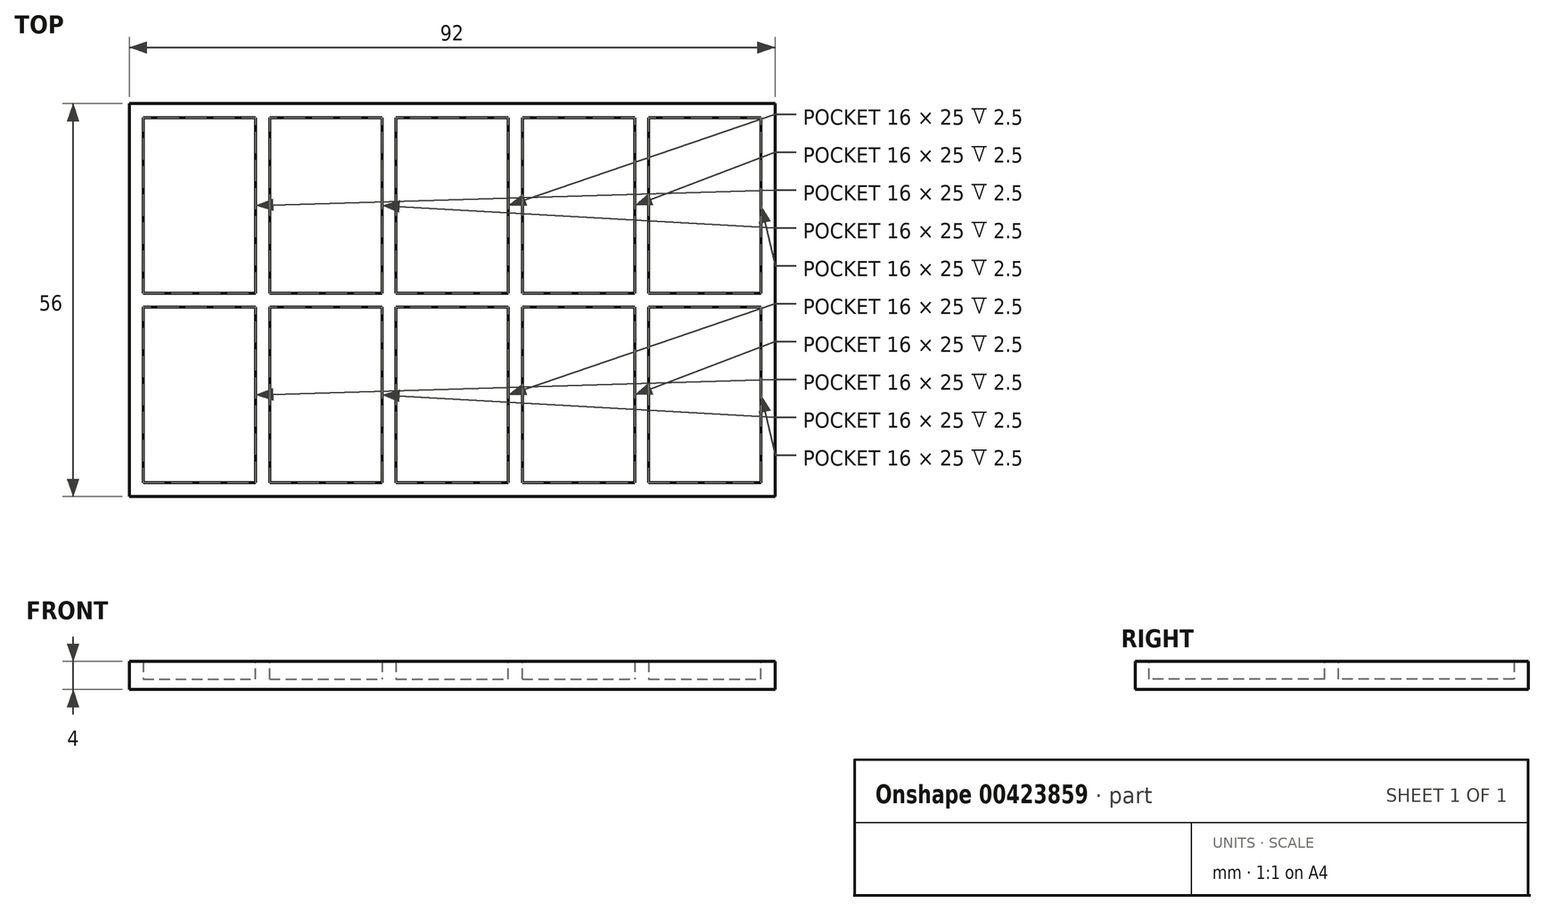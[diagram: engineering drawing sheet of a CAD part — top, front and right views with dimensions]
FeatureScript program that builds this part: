
annotation { "Feature Type Name" : "Feature", "Feature Type Description" : "" }
export const myFeature = defineFeature(function(context is Context, id is Id, definition is map)
    precondition{}
    {
        {
            var Q0;
            Q0=qCreatedBy(makeId("Top.planeOp"),FACE);
            var sketch = newSketch(context, id + "F0", { "sketchPlane" : qUnion([Q0])});
            skLineSegment(sketch, "E0.bottom", {"start": v(46, 28) * mm, "end": v(-46, 28) * mm});
            skLineSegment(sketch, "E0.top", {"start": v(46, -28) * mm, "end": v(-46, -28) * mm});
            skLineSegment(sketch, "E0.left", {"start": v(46, 28) * mm, "end": v(46, -28) * mm});
            skLineSegment(sketch, "E0.right", {"start": v(-46, 28) * mm, "end": v(-46, -28) * mm});
            skPoint(sketch, "E0.middle", {"position": v(0, 0) * mm});
            skSolve(sketch);
        }
        {
            var Q0;
            Q0=makeQuery(id+"F0.imprint","IMPRINT",FACE,{"disambiguationData":[TD([[makeQuery(id+"F0.imprint","IMPRINT",EDGE,{"derivedFrom":sQuery(id+"F0.wireOp",EDGE,"E0.bottom")}),1.0]])]});
            var Q1;
            Q1 = qSketchRegion(id + "F2", true);
            extrude(context, id + "F1", {"entities" : qUnion([Q0, Q1]), "depth" : 1.5 * mm, "offsetDistance" : 25 * mm});
        }
        {
            var Q0;
            Q0=qCreatedBy(makeId("Top.planeOp"),FACE);
            var sketch = newSketch(context, id + "F2", { "sketchPlane" : qUnion([Q0])});
            skLineSegment(sketch, "E1.bottom", {"start": v(46, -28) * mm, "end": v(44, -28) * mm});
            skLineSegment(sketch, "E1.top", {"start": v(46, 28) * mm, "end": v(44, 28) * mm});
            skLineSegment(sketch, "E1.left", {"start": v(46, -28) * mm, "end": v(46, 28) * mm});
            skLineSegment(sketch, "E1.right", {"start": v(44, -28) * mm, "end": v(44, 28) * mm});
            skSolve(sketch);
        }
        {
            var Q0;
            Q0 = qSketchRegion(id + "F2", true);
            extrude(context, id + "F3", {"entities" : qUnion([Q0]), "depth" : 4 * mm, "offsetDistance" : 25 * mm});
        }
        {
            var Q0;
            Q0=makeQuery(id+"F3.opExtrude","SWEPT_BODY",BODY,{"disambiguationData":[OSD([sQuery(id+"F2.wireOp",EDGE,"E1.bottom"),sQuery(id+"F2.wireOp",EDGE,"E1.top"),sQuery(id+"F2.wireOp",EDGE,"E1.left"),sQuery(id+"F2.wireOp",EDGE,"E1.right")])]});
            var Q1;
            Q1=qCreatedBy(makeId("Right.planeOp"),FACE);
            mirror(context, id + "F4", {"operationType" : NewBodyOperationType.ADD, "entities" : qUnion([Q0]), "mirrorPlane" : qUnion([Q1])});
        }
        {
            var Q0;
            Q0=qCreatedBy(makeId("Top.planeOp"),FACE);
            var sketch = newSketch(context, id + "F5", { "sketchPlane" : qUnion([Q0])});
            skLineSegment(sketch, "E2.bottom", {"start": v(-46, -28) * mm, "end": v(46, -28) * mm});
            skLineSegment(sketch, "E2.top", {"start": v(-46, -26) * mm, "end": v(46, -26) * mm});
            skLineSegment(sketch, "E2.left", {"start": v(-46, -28) * mm, "end": v(-46, -26) * mm});
            skLineSegment(sketch, "E2.right", {"start": v(46, -28) * mm, "end": v(46, -26) * mm});
            skSolve(sketch);
        }
        {
            var Q0;
            Q0 = qSketchRegion(id + "F5", true);
            extrude(context, id + "F6", {"entities" : qUnion([Q0]), "operationType" : NewBodyOperationType.ADD, "depth" : 4 * mm, "offsetDistance" : 25 * mm});
        }
        {
            var Q0;
            Q0=makeQuery(id+"F1.opExtrude","SWEPT_BODY",BODY,{"disambiguationData":[OSD([sQuery(id+"F0.wireOp",EDGE,"E0.bottom"),sQuery(id+"F0.wireOp",EDGE,"E0.top"),sQuery(id+"F0.wireOp",EDGE,"E0.left"),sQuery(id+"F0.wireOp",EDGE,"E0.right")])]});
            var Q1;
            Q1=qCreatedBy(makeId("Front.planeOp"),FACE);
            mirror(context, id + "F7", {"operationType" : NewBodyOperationType.ADD, "entities" : qUnion([Q0]), "mirrorPlane" : qUnion([Q1])});
        }
        {
            var Q0;
            Q0=qCreatedBy(makeId("Top.planeOp"),FACE);
            var sketch = newSketch(context, id + "F8", { "sketchPlane" : qUnion([Q0])});
            skLineSegment(sketch, "E3.bottom", {"start": v(26, 28) * mm, "end": v(28, 28) * mm});
            skLineSegment(sketch, "E3.top", {"start": v(26, -28) * mm, "end": v(28, -28) * mm});
            skLineSegment(sketch, "E3.left", {"start": v(26, 28) * mm, "end": v(26, -28) * mm});
            skLineSegment(sketch, "E3.right", {"start": v(28, 28) * mm, "end": v(28, -28) * mm});
            skSolve(sketch);
        }
        {
            var Q0;
            Q0=makeQuery(id+"F8.imprint","IMPRINT",FACE,{"disambiguationData":[TD([[makeQuery(id+"F8.imprint","IMPRINT",EDGE,{"derivedFrom":sQuery(id+"F8.wireOp",EDGE,"E3.bottom")}),-1.0]])]});
            extrude(context, id + "F9", {"entities" : qUnion([Q0]), "operationType" : NewBodyOperationType.ADD, "depth" : 4 * mm, "offsetDistance" : 25 * mm});
        }
        {
            var Q0;
            Q0=makeQuery(id+"F1.opExtrude","SWEPT_BODY",BODY,{"disambiguationData":[OSD([sQuery(id+"F0.wireOp",EDGE,"E0.bottom"),sQuery(id+"F0.wireOp",EDGE,"E0.top"),sQuery(id+"F0.wireOp",EDGE,"E0.left"),sQuery(id+"F0.wireOp",EDGE,"E0.right")])]});
            var Q1;
            Q1=qCreatedBy(makeId("Right.planeOp"),FACE);
            mirror(context, id + "F10", {"operationType" : NewBodyOperationType.ADD, "entities" : qUnion([Q0]), "mirrorPlane" : qUnion([Q1])});
        }
        {
            var Q0;
            Q0=qCreatedBy(makeId("Top.planeOp"),FACE);
            var sketch = newSketch(context, id + "F11", { "sketchPlane" : qUnion([Q0])});
            skLineSegment(sketch, "E4.bottom", {"start": v(8, -28) * mm, "end": v(10, -28) * mm});
            skLineSegment(sketch, "E4.top", {"start": v(8, 28) * mm, "end": v(10, 28) * mm});
            skLineSegment(sketch, "E4.left", {"start": v(8, -28) * mm, "end": v(8, 28) * mm});
            skLineSegment(sketch, "E4.right", {"start": v(10, -28) * mm, "end": v(10, 28) * mm});
            skSolve(sketch);
        }
        {
            var Q0;
            Q0 = qSketchRegion(id + "F11", true);
            var Q1;
            Q1 = qSketchRegion(id + "F14", true);
            extrude(context, id + "F12", {"entities" : qUnion([Q0, Q1]), "operationType" : NewBodyOperationType.ADD, "depth" : 4 * mm, "offsetDistance" : 25 * mm});
        }
        {
            var Q0;
            Q0=makeQuery(id+"F1.opExtrude","SWEPT_BODY",BODY,{"disambiguationData":[OSD([sQuery(id+"F0.wireOp",EDGE,"E0.bottom"),sQuery(id+"F0.wireOp",EDGE,"E0.top"),sQuery(id+"F0.wireOp",EDGE,"E0.left"),sQuery(id+"F0.wireOp",EDGE,"E0.right")])]});
            var Q1;
            Q1=qCreatedBy(makeId("Right.planeOp"),FACE);
            mirror(context, id + "F13", {"operationType" : NewBodyOperationType.ADD, "entities" : qUnion([Q0]), "mirrorPlane" : qUnion([Q1])});
        }
        {
            var Q0;
            Q0=qCreatedBy(makeId("Top.planeOp"),FACE);
            var sketch = newSketch(context, id + "F14", { "sketchPlane" : qUnion([Q0])});
            skLineSegment(sketch, "E5.bottom", {"start": v(46, -1) * mm, "end": v(-46, -1) * mm});
            skLineSegment(sketch, "E5.top", {"start": v(46, 1) * mm, "end": v(-46, 1) * mm});
            skLineSegment(sketch, "E5.left", {"start": v(46, -1) * mm, "end": v(46, 1) * mm});
            skLineSegment(sketch, "E5.right", {"start": v(-46, -1) * mm, "end": v(-46, 1) * mm});
            skSolve(sketch);
        }
        {
            var Q0;
            Q0 = qSketchRegion(id + "F14", true);
            extrude(context, id + "F15", {"entities" : qUnion([Q0]), "operationType" : NewBodyOperationType.ADD, "depth" : 4 * mm, "offsetDistance" : 25 * mm});
        }
    });
